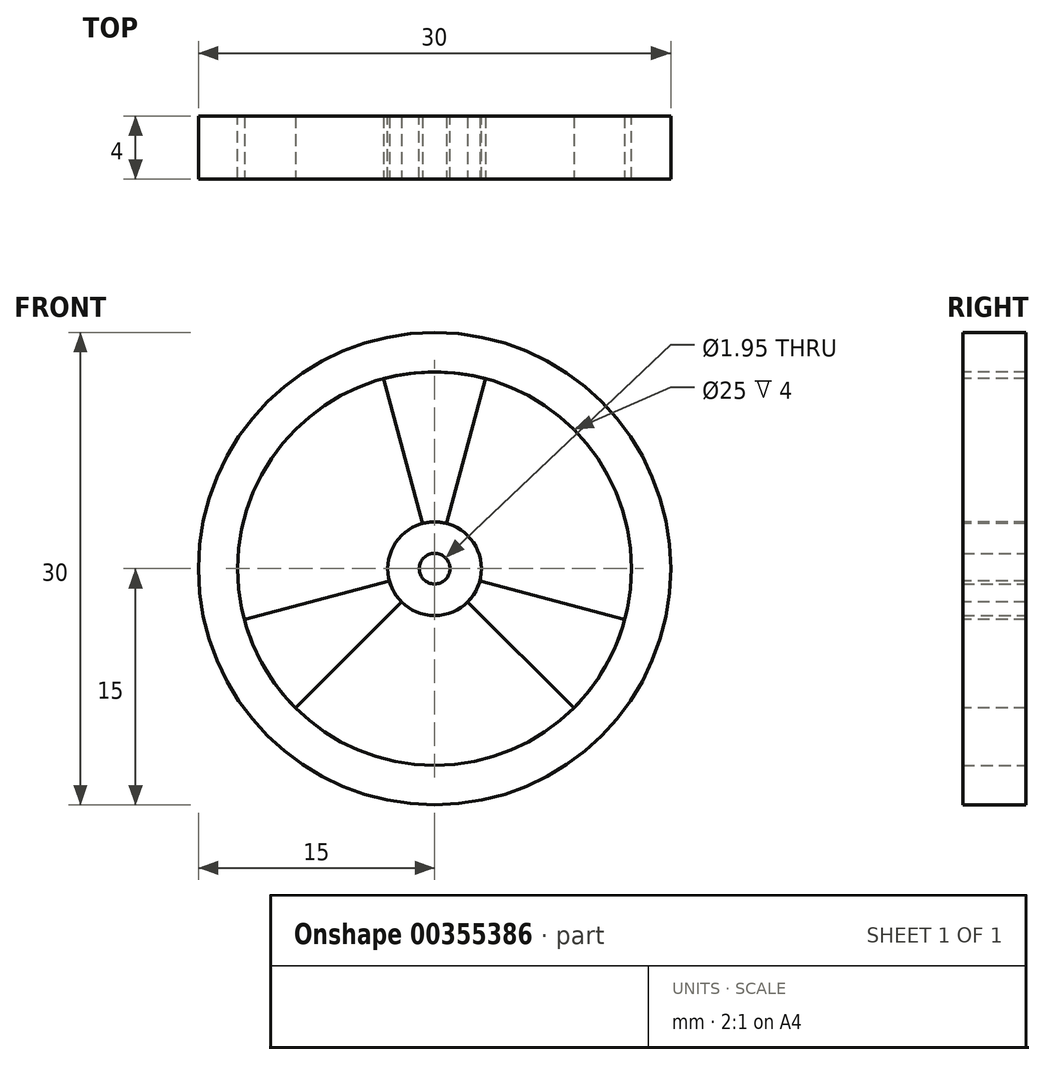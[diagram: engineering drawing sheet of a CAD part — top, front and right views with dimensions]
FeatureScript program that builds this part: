
annotation { "Feature Type Name" : "Feature", "Feature Type Description" : "" }
export const myFeature = defineFeature(function(context is Context, id is Id, definition is map)
    precondition{}
    {
        {
            var Q0;
            Q0=qCreatedBy(makeId("Front.planeOp"),FACE);
            var sketch = newSketch(context, id + "F0", { "sketchPlane" : qUnion([Q0])});
            skCircle(sketch, "E0", {"center": v(0, 0) * mm, "radius": 15 * mm});
            skCircle(sketch, "E1", {"center": v(0, 0) * mm, "radius": 0.97 * mm});
            skCircle(sketch, "E2", {"center": v(0, 0) * mm, "radius": 2.98 * mm});
            skCircle(sketch, "E3", {"center": v(0, 0) * mm, "radius": 12.5 * mm});
            skSolve(sketch);
        }
        {
            var Q0;
            Q0 = qSketchRegion(id + "F0", true);
            var Q1;
            Q1=makeQuery(id+"F0.imprint","IMPRINT",FACE,{"disambiguationData":[TD([[makeQuery(id+"F0.imprint","IMPRINT",EDGE,{"derivedFrom":sQuery(id+"F0.wireOp",EDGE,"E1")}),-1.0]])]});
            extrude(context, id + "F1", {"entities" : qUnion([Q0, Q1]), "depth" : 4 * mm});
        }
        {
            var Q0;
            Q0=makeQuery(id+"F1.opExtrude","CAP_FACE",FACE,{"disambiguationData":[OSD([sQuery(id+"F0.wireOp",EDGE,"E0"),sQuery(id+"F0.wireOp",EDGE,"E1")])],"isStart":false});
            var sketch = newSketch(context, id + "F2", { "sketchPlane" : qUnion([Q0])});
            skArc(sketch, "E4", {"start": v(0.77, 2.87) * mm, "mid": v(0, 2.98) * mm, "end": v(-0.77, 2.87) * mm});
            skArc(sketch, "E5", {"start": v(3.24, 12.07) * mm, "mid": v(0, 12.5) * mm, "end": v(-3.24, 12.07) * mm});
            skLineSegment(sketch, "E6", {"start": v(0.77, 2.87) * mm, "end": v(3.24, 12.07) * mm});
            skLineSegment(sketch, "E7", {"start": v(3.24, 12.07) * mm, "end": v(0.77, 2.87) * mm});
            skLineSegment(sketch, "E8", {"start": v(-0.77, 2.87) * mm, "end": v(-3.24, 12.07) * mm});
            skSolve(sketch);
        }
        {
            var Q0;
            Q0 = qSketchRegion(id + "F2", true);
            extrude(context, id + "F3", {"entities" : qUnion([Q0]), "oppositeDirection" : true, "depth" : 4 * mm});
        }
        {
            var Q0;
            Q0=makeQuery(id+"F3.opExtrude","SWEPT_BODY",BODY,{"disambiguationData":[OSD([sQuery(id+"F2.wireOp",EDGE,"E4"),sQuery(id+"F2.wireOp",EDGE,"E5"),sQuery(id+"F2.wireOp",EDGE,"E7"),sQuery(id+"F2.wireOp",EDGE,"E8")])]});
            var Q1;
            Q1=makeQuery(id+"F1.opExtrude","CAP_EDGE",EDGE,{"disambiguationData":[OSD([sQuery(id+"F0.wireOp",EDGE,"E2")])],"isStart":true});
            circularPattern(context, id + "F4", {"entities" : qUnion([Q0]), "axis" : qUnion([Q1]), "angle" : 360 * degree, "instanceCount" : 3, "equalSpace" : true});
        }
    });
